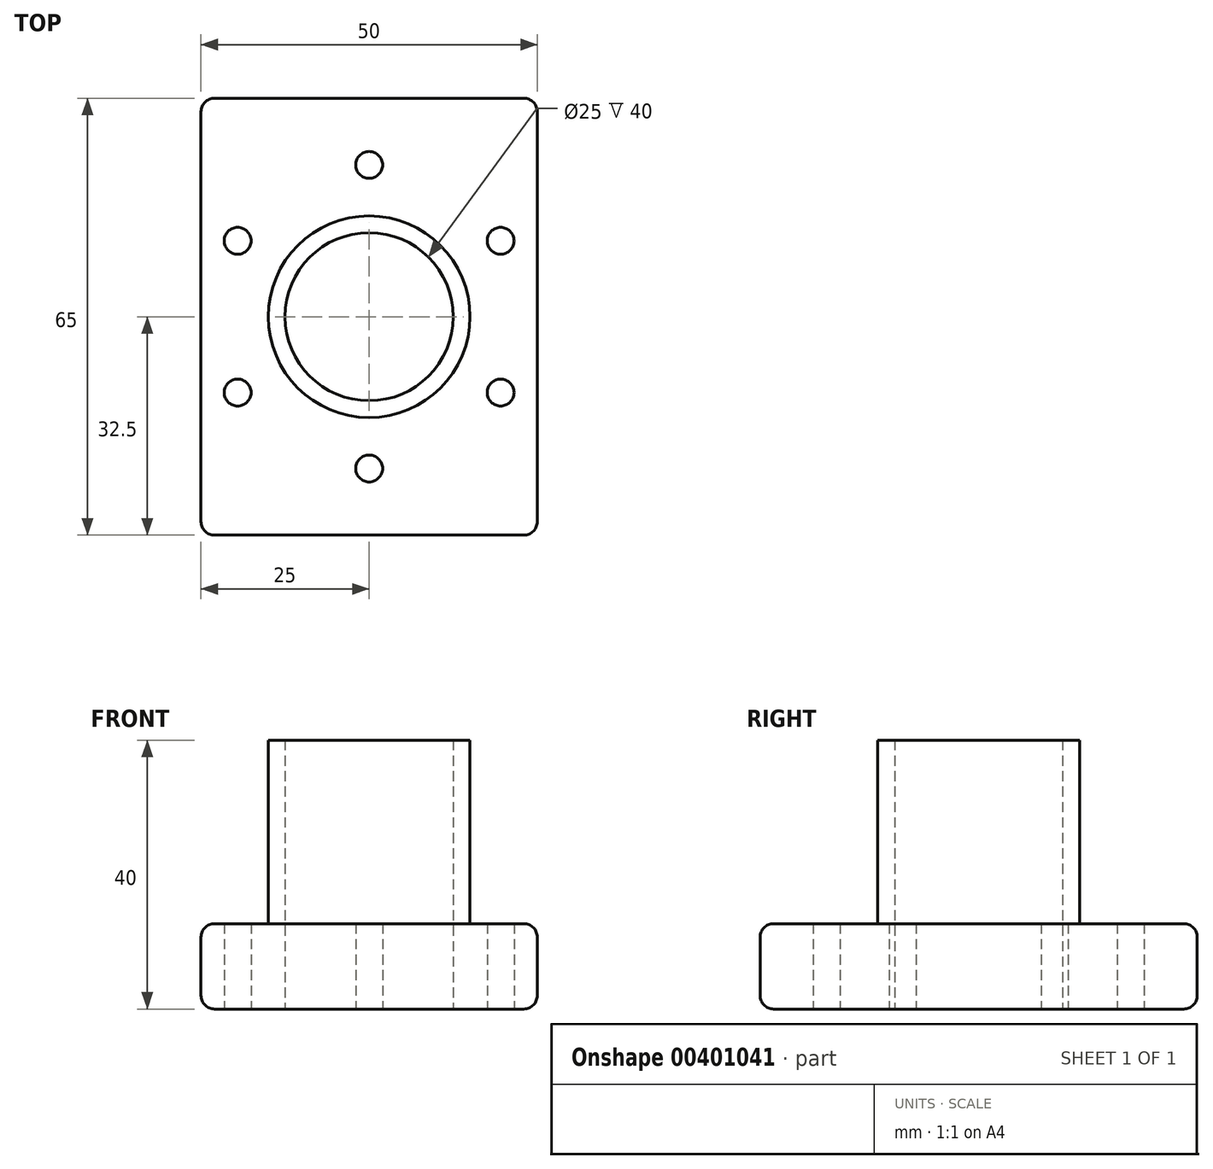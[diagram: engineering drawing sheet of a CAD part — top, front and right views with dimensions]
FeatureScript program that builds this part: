
annotation { "Feature Type Name" : "Feature", "Feature Type Description" : "" }
export const myFeature = defineFeature(function(context is Context, id is Id, definition is map)
    precondition{}
    {
        {
            var Q0;
            Q0=qCreatedBy(makeId("Top.planeOp"),FACE);
            var sketch = newSketch(context, id + "F0", { "sketchPlane" : qUnion([Q0])});
            skLineSegment(sketch, "E0.bottom", {"start": v(-25, 32.5) * mm, "end": v(25, 32.5) * mm});
            skLineSegment(sketch, "E0.top", {"start": v(-25, -32.5) * mm, "end": v(25, -32.5) * mm});
            skLineSegment(sketch, "E0.left", {"start": v(-25, 32.5) * mm, "end": v(-25, -32.5) * mm});
            skLineSegment(sketch, "E0.right", {"start": v(25, 32.5) * mm, "end": v(25, -32.5) * mm});
            skCircle(sketch, "E1", {"center": v(0, 0) * mm, "radius": 15 * mm});
            skCircle(sketch, "E2", {"center": v(0, 22.58) * mm, "radius": 2 * mm});
            skCircle(sketch, "E3.1.0", {"center": v(-19.56, 11.3) * mm, "radius": 2 * mm});
            skCircle(sketch, "E3.2.0", {"center": v(-19.56, -11.3) * mm, "radius": 2 * mm});
            skCircle(sketch, "E3.3.0", {"center": v(0, -22.58) * mm, "radius": 2 * mm});
            skCircle(sketch, "E3.4.0", {"center": v(19.56, -11.3) * mm, "radius": 2 * mm});
            skCircle(sketch, "E3.5.0", {"center": v(19.56, 11.3) * mm, "radius": 2 * mm});
            skCircle(sketch, "E4", {"center": v(0, 0) * mm, "radius": 12.5 * mm});
            skSolve(sketch);
        }
        {
            var Q0;
            Q0=makeQuery(id+"F0.imprint","IMPRINT",FACE,{"disambiguationData":[TD([[makeQuery(id+"F0.imprint","IMPRINT",EDGE,{"derivedFrom":sQuery(id+"F0.wireOp",EDGE,"E0.bottom")}),-1.0]])]});
            extrude(context, id + "F1", {"entities" : qUnion([Q0]), "depth" : 12.7 * mm});
        }
        {
            var Q0;
            Q0=makeQuery(id+"F1.opExtrude","SWEPT_FACE",FACE,{"disambiguationData":[OSD([sQuery(id+"F0.wireOp",EDGE,"E0.left")])]});
            var Q1;
            Q1=makeQuery(id+"F1.opExtrude","SWEPT_FACE",FACE,{"disambiguationData":[OSD([sQuery(id+"F0.wireOp",EDGE,"E0.top")])]});
            var Q2;
            Q2=makeQuery(id+"F1.opExtrude","SWEPT_FACE",FACE,{"disambiguationData":[OSD([sQuery(id+"F0.wireOp",EDGE,"E0.right")])]});
            var Q3;
            Q3=makeQuery(id+"F1.opExtrude","SWEPT_FACE",FACE,{"disambiguationData":[OSD([sQuery(id+"F0.wireOp",EDGE,"E0.bottom")])]});
            fillet(context, id + "F2", {"entities" : qUnion([Q0, Q1, Q2, Q3]), "radius" : 2 * mm, "tangentPropagation" : true, "allowEdgeOverflow" : false});
        }
        {
            var Q0;
            Q0=makeQuery(id+"F0.imprint","IMPRINT",FACE,{"disambiguationData":[TD([[makeQuery(id+"F0.imprint","IMPRINT",EDGE,{"derivedFrom":sQuery(id+"F0.wireOp",EDGE,"E1")}),1.0]])]});
            extrude(context, id + "F3", {"entities" : qUnion([Q0]), "operationType" : NewBodyOperationType.ADD, "depth" : 40 * mm});
        }
    });
